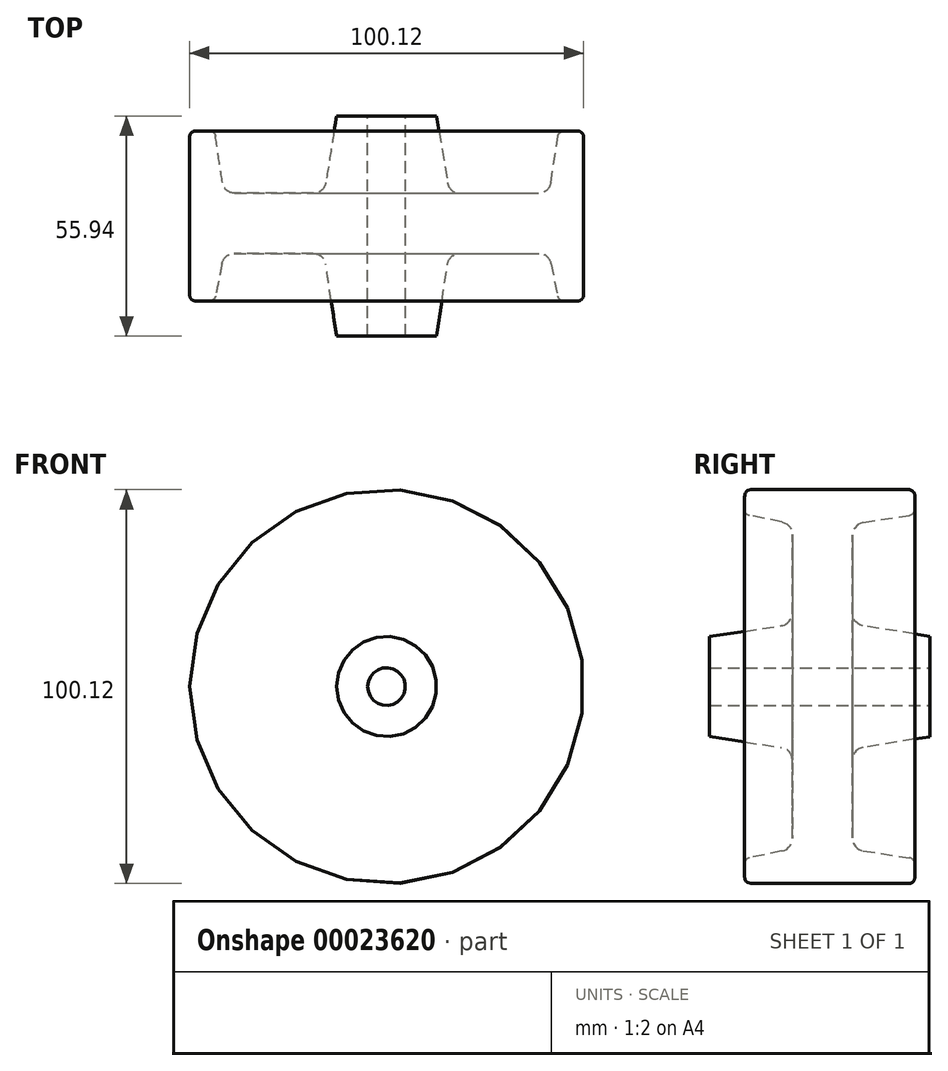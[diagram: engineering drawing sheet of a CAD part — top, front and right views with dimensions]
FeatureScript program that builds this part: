
annotation { "Feature Type Name" : "Feature", "Feature Type Description" : "" }
export const myFeature = defineFeature(function(context is Context, id is Id, definition is map)
    precondition{}
    {
        {
            var Q0;
            Q0=qCreatedBy(makeId("Top.planeOp"),FACE);
            var sketch = newSketch(context, id + "F0", { "sketchPlane" : qUnion([Q0])});
            skLineSegment(sketch, "E0.left", {"start": v(-27, 31.79) * mm, "end": v(-27, -24.14) * mm});
            skLineSegment(sketch, "E1", {"start": v(-27, 31.79) * mm, "end": v(-34.93, 31.79) * mm});
            skLineSegment(sketch, "E2", {"start": v(-27, -24.14) * mm, "end": v(-34.93, -24.14) * mm});
            skLineSegment(sketch, "E3", {"start": v(-27, 12.15) * mm, "end": v(-38.1, 12.15) * mm});
            skLineSegment(sketch, "E4", {"start": v(-38.1, -3.16) * mm, "end": v(-27, -3.16) * mm});
            skLineSegment(sketch, "E5", {"start": v(-34.93, 31.79) * mm, "end": v(-37.67, 14.82) * mm});
            skLineSegment(sketch, "E6", {"start": v(-34.93, -24.14) * mm, "end": v(-37.7, -5.86) * mm});
            skLineSegment(sketch, "E7", {"start": v(-40.83, -3.16) * mm, "end": v(-60.9, -3.16) * mm});
            skLineSegment(sketch, "E8", {"start": v(-40.8, 12.15) * mm, "end": v(-60.78, 12.15) * mm});
            skLineSegment(sketch, "E9", {"start": v(-72.26, 26.4) * mm, "end": v(-72.26, -13.65) * mm});
            skLineSegment(sketch, "E10", {"start": v(-70.68, -15.24) * mm, "end": v(-67.22, -15.24) * mm});
            skLineSegment(sketch, "E11", {"start": v(-70.68, 28) * mm, "end": v(-67.28, 28) * mm});
            skLineSegment(sketch, "E12", {"start": v(-65.7, 26.64) * mm, "end": v(-63.91, 14.85) * mm});
            skLineSegment(sketch, "E13", {"start": v(-65.66, -13.96) * mm, "end": v(-64.01, -5.72) * mm});
            skPoint(sketch, "E14.visualSharp", {"position": v(-63.5, -3.16) * mm});
            skArc(sketch, "E14.filletArc", {"start": v(-60.9, -3.16) * mm, "mid": v(-62.91, -3.88) * mm, "end": v(-64.01, -5.72) * mm});
            skPoint(sketch, "E15.visualSharp", {"position": v(-63.5, 12.15) * mm});
            skArc(sketch, "E15.filletArc", {"start": v(-63.91, 14.85) * mm, "mid": v(-62.85, 12.92) * mm, "end": v(-60.78, 12.15) * mm});
            skPoint(sketch, "E16.visualSharp", {"position": v(-38.1, 12.15) * mm});
            skArc(sketch, "E16.filletArc", {"start": v(-40.8, 12.15) * mm, "mid": v(-38.75, 12.9) * mm, "end": v(-37.67, 14.82) * mm});
            skPoint(sketch, "E17.visualSharp", {"position": v(-38.1, -3.16) * mm});
            skArc(sketch, "E17.filletArc", {"start": v(-37.7, -5.86) * mm, "mid": v(-38.76, -3.93) * mm, "end": v(-40.83, -3.16) * mm});
            skPoint(sketch, "E18.visualSharp", {"position": v(-72.26, 28) * mm});
            skArc(sketch, "E18.filletArc", {"start": v(-70.68, 28) * mm, "mid": v(-71.8, 27.53) * mm, "end": v(-72.26, 26.4) * mm});
            skPoint(sketch, "E19.visualSharp", {"position": v(-72.26, -15.24) * mm});
            skArc(sketch, "E19.filletArc", {"start": v(-72.26, -13.65) * mm, "mid": v(-71.8, -14.78) * mm, "end": v(-70.68, -15.24) * mm});
            skPoint(sketch, "E20.visualSharp", {"position": v(-65.91, -15.24) * mm});
            skArc(sketch, "E20.filletArc", {"start": v(-67.22, -15.24) * mm, "mid": v(-66.2, -14.88) * mm, "end": v(-65.66, -13.96) * mm});
            skPoint(sketch, "E21.visualSharp", {"position": v(-65.91, 28) * mm});
            skArc(sketch, "E21.filletArc", {"start": v(-65.7, 26.64) * mm, "mid": v(-66.24, 27.6) * mm, "end": v(-67.28, 28) * mm});
            skLineSegment(sketch, "E22", {"start": v(-22.2, 26.66) * mm, "end": v(-22.22, -24.14) * mm});
            skLineSegment(sketch, "E23", {"start": v(-65.91, -15.24) * mm, "end": v(-65.91, -24.14) * mm});
            skSolve(sketch);
        }
        {
            var Q0;
            {var subQ1=sQuery(id+"F0.wireOp",EDGE,"E1");Q0=makeQuery(id+"F0.imprint","IMPRINT",FACE,{"disambiguationData":[TD([[makeQuery(id+"F0.imprint","IMPRINT",EDGE,{"derivedFrom":subQ1}),1.0]])]});}
            var Q1;
            Q1=sQuery(id+"F0.wireOp",EDGE,"E22");
            revolve(context, id + "F1", {"entities" : qUnion([Q0]), "axis" : qUnion([Q1]), "revolveType" : RevolveType.FULL});
        }
    });
